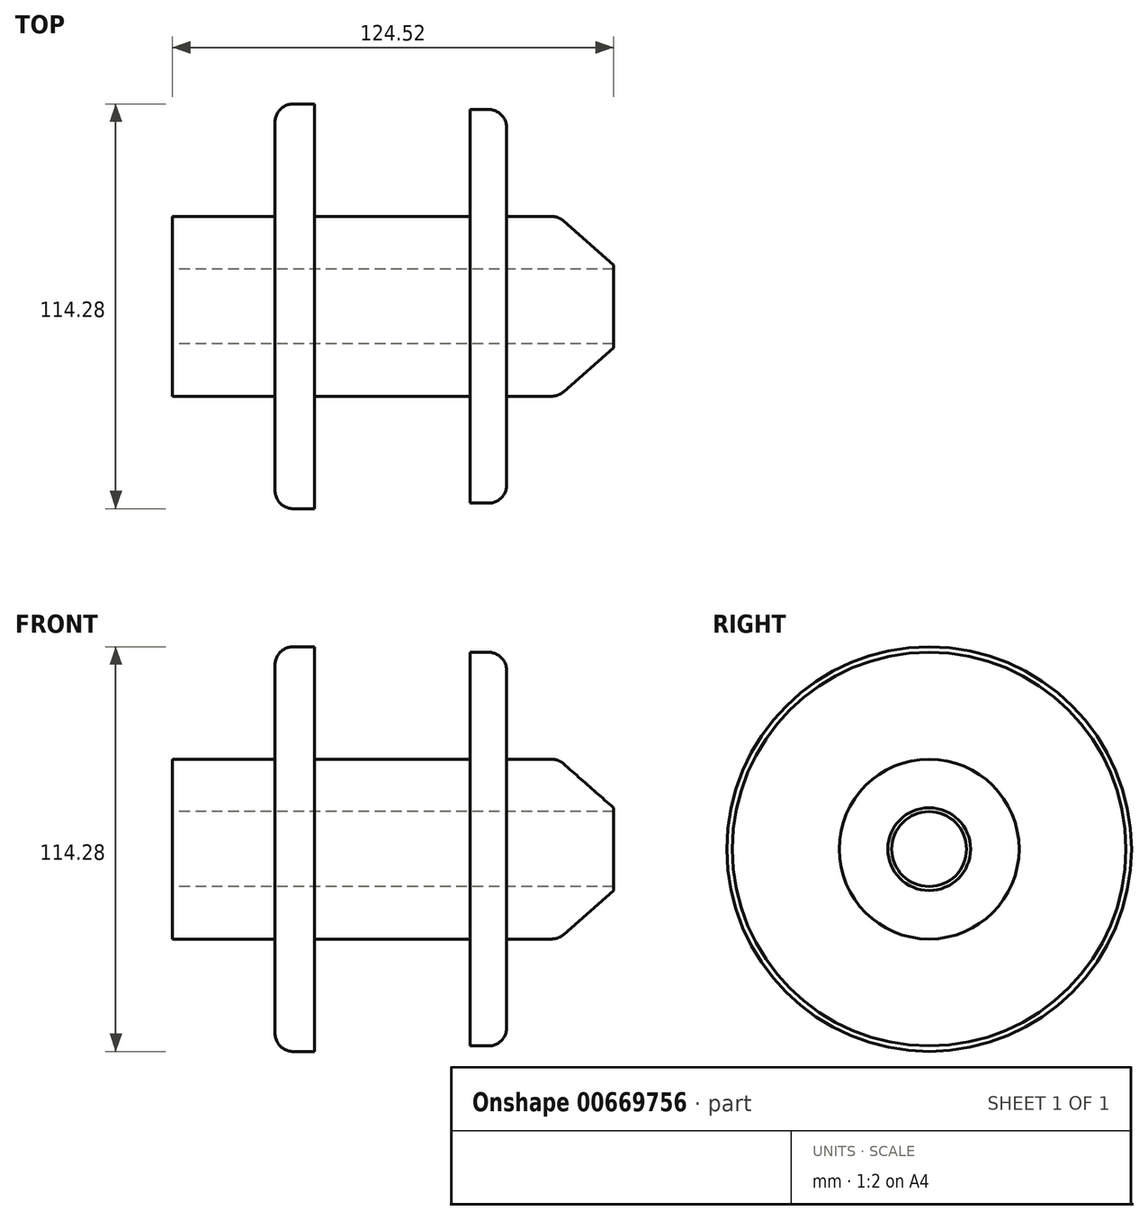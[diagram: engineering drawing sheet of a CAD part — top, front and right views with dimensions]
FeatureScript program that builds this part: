
annotation { "Feature Type Name" : "Feature", "Feature Type Description" : "" }
export const myFeature = defineFeature(function(context is Context, id is Id, definition is map)
    precondition{}
    {
        {
            var Q0;
            Q0=qCreatedBy(makeId("Front.planeOp"),FACE);
            var sketch = newSketch(context, id + "F0", { "sketchPlane" : qUnion([Q0])});
            skLineSegment(sketch, "E0", {"start": v(0, 0) * mm, "end": v(124.52, 0) * mm});
            skLineSegment(sketch, "E1", {"start": v(124.52, 0) * mm, "end": v(124.52, 11.69) * mm});
            skLineSegment(sketch, "E2", {"start": v(124.52, 11.69) * mm, "end": v(108.96, 25.38) * mm});
            skLineSegment(sketch, "E3", {"start": v(108.96, 25.38) * mm, "end": v(94.33, 25.38) * mm});
            skLineSegment(sketch, "E4", {"start": v(94.33, 25.38) * mm, "end": v(94.33, 55.58) * mm});
            skLineSegment(sketch, "E5", {"start": v(94.33, 55.58) * mm, "end": v(84.05, 55.58) * mm});
            skLineSegment(sketch, "E6", {"start": v(84.05, 55.58) * mm, "end": v(84.05, 25.38) * mm});
            skLineSegment(sketch, "E7", {"start": v(84.05, 25.38) * mm, "end": v(40.16, 25.38) * mm});
            skLineSegment(sketch, "E8", {"start": v(40.16, 25.38) * mm, "end": v(40.16, 57.14) * mm});
            skLineSegment(sketch, "E9", {"start": v(40.16, 57.14) * mm, "end": v(28.95, 57.14) * mm});
            skLineSegment(sketch, "E10", {"start": v(28.95, 57.14) * mm, "end": v(28.95, 25.38) * mm});
            skLineSegment(sketch, "E11", {"start": v(28.95, 25.38) * mm, "end": v(0, 25.38) * mm});
            skLineSegment(sketch, "E12", {"start": v(0, 25.38) * mm, "end": v(0, 0) * mm});
            skSolve(sketch);
        }
        {
            var Q0;
            Q0 = qSketchRegion(id + "FvQedC5hWsqpyRL_0", true);
            var Q1;
            Q1=makeQuery(id+"F0.imprint","IMPRINT",FACE,{"disambiguationData":[TD([[makeQuery(id+"F0.imprint","IMPRINT",EDGE,{"derivedFrom":sQuery(id+"F0.wireOp",EDGE,"E0")}),1.0]])]});
            var Q2;
            Q2=sQuery(id+"F0.wireOp",EDGE,"E0");
            revolve(context, id + "F1", {"entities" : qUnion([Q0, Q1]), "axis" : qUnion([Q2]), "revolveType" : RevolveType.FULL});
        }
        {
            var Q0;
            Q0=qCreatedBy(makeId("Right.planeOp"),FACE);
            var sketch = newSketch(context, id + "F2", { "sketchPlane" : qUnion([Q0])});
            skCircle(sketch, "E13", {"center": v(0, 0) * mm, "radius": 10.57 * mm});
            skSolve(sketch);
        }
        {
            var Q0;
            Q0=makeQuery(id+"F2.imprint","IMPRINT",FACE,{"disambiguationData":[TD([[makeQuery(id+"F2.imprint","IMPRINT",EDGE,{"derivedFrom":sQuery(id+"F2.wireOp",EDGE,"E13")}),1.0]])]});
            extrude(context, id + "F3", {"entities" : qUnion([Q0]), "operationType" : NewBodyOperationType.REMOVE, "endBound" : BoundingType.THROUGH_ALL, "depth" : 25.4 * mm, "offsetDistance" : 25.4 * mm});
        }
        {
            var Q0;
            Q0=makeQuery(id+"F1.opRevolve","SWEPT_EDGE",EDGE,{"disambiguationData":[OSD([sQuery(id+"F0.wireOp",EDGE,"E2"),sQuery(id+"F0.wireOp",EDGE,"E3")])]});
            var Q1;
            Q1=makeQuery(id+"F1.opRevolve","SWEPT_EDGE",EDGE,{"disambiguationData":[OSD([sQuery(id+"F0.wireOp",EDGE,"E4"),sQuery(id+"F0.wireOp",EDGE,"E5")])]});
            var Q2;
            Q2=makeQuery(id+"F1.opRevolve","SWEPT_EDGE",EDGE,{"disambiguationData":[OSD([sQuery(id+"F0.wireOp",EDGE,"E9"),sQuery(id+"F0.wireOp",EDGE,"E10")])]});
            fillet(context, id + "F4", {"entities" : qUnion([Q0, Q1, Q2]), "radius" : 5.08 * mm, "tangentPropagation" : true, "allowEdgeOverflow" : false});
        }
    });
